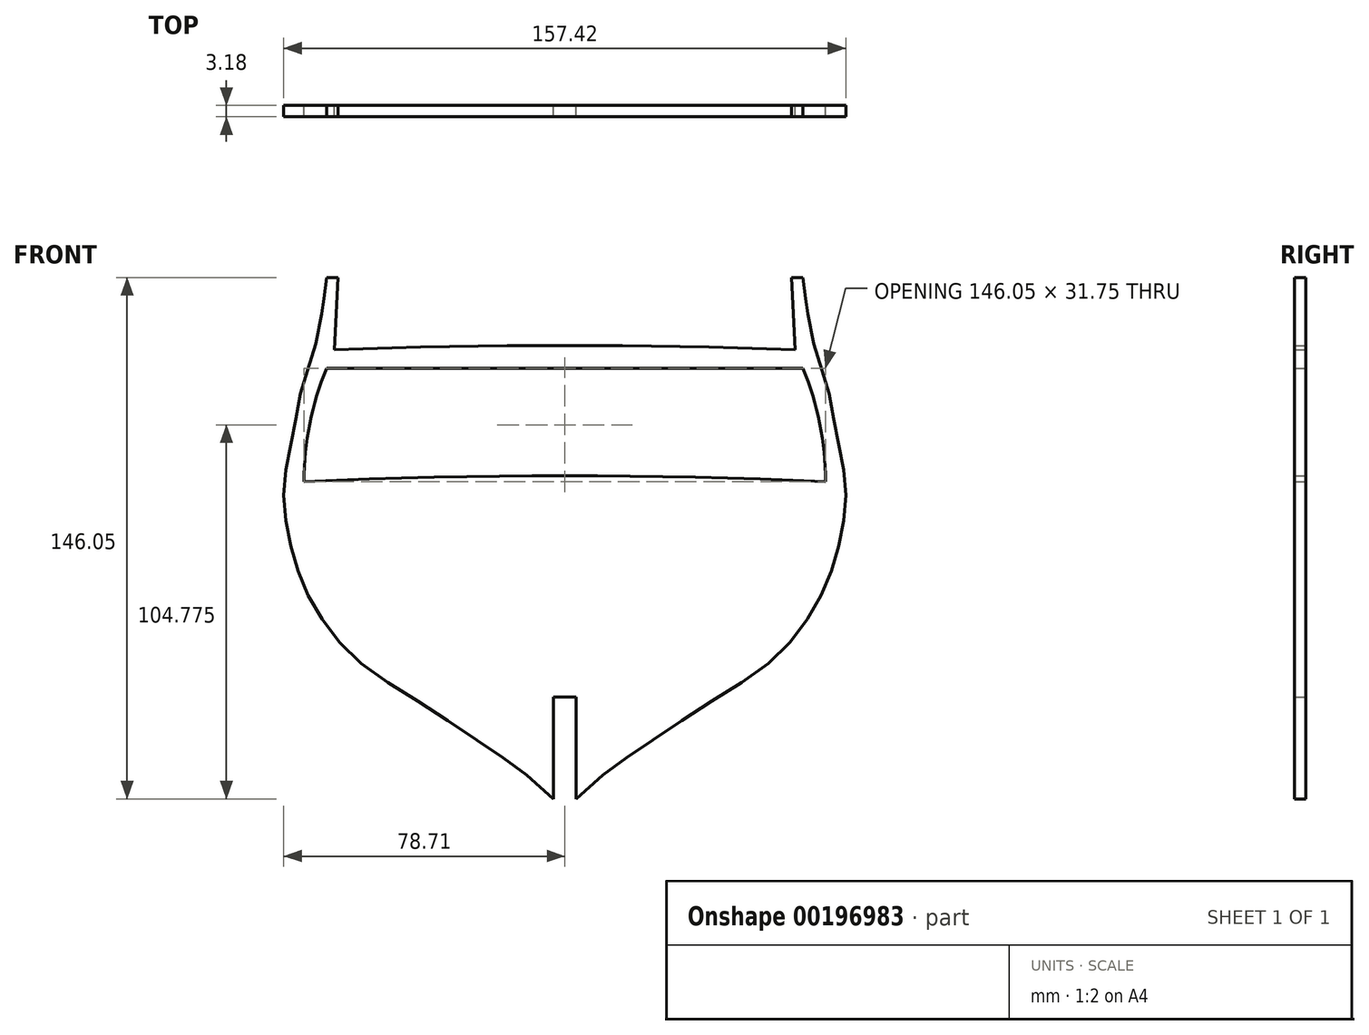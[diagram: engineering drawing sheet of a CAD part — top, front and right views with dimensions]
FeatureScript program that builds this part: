
annotation { "Feature Type Name" : "Feature", "Feature Type Description" : "" }
export const myFeature = defineFeature(function(context is Context, id is Id, definition is map)
    precondition{}
    {
        {
            var Q0;
            Q0=qCreatedBy(makeId("Front.planeOp"),FACE);
            var sketch = newSketch(context, id + "F0", { "sketchPlane" : qUnion([Q0])});
            skLineSegment(sketch, "E0", {"start": v(0, 0) * mm, "end": v(0, -60.33) * mm, "construction": true});
            skLineSegment(sketch, "E1", {"start": v(0, -60.33) * mm, "end": v(3.18, -60.33) * mm});
            skLineSegment(sketch, "E2", {"start": v(3.18, -60.33) * mm, "end": v(3.18, -88.9) * mm});
            skLineSegment(sketch, "E3", {"start": v(3.18, -88.9) * mm, "end": v(-3.18, -88.9) * mm, "construction": true});
            skLineSegment(sketch, "E4", {"start": v(-3.18, -88.9) * mm, "end": v(-3.18, -60.33) * mm});
            skLineSegment(sketch, "E5", {"start": v(-3.18, -60.33) * mm, "end": v(0, -60.33) * mm});
            skLineSegment(sketch, "E6", {"start": v(0, 0) * mm, "end": v(0, 31.75) * mm, "construction": true});
            skLineSegment(sketch, "E7", {"start": v(0, 31.75) * mm, "end": v(0, 38.1) * mm, "construction": true});
            skLineSegment(sketch, "E8", {"start": v(0, 31.75) * mm, "end": v(66.68, 31.75) * mm});
            skLineSegment(sketch, "E9", {"start": v(66.68, 31.75) * mm, "end": v(73.03, 0) * mm, "construction": true});
            skLineSegment(sketch, "E10", {"start": v(73.03, 0) * mm, "end": v(0, 0) * mm, "construction": true});
            skLineSegment(sketch, "E11", {"start": v(0, 0) * mm, "end": v(-73.03, 0) * mm, "construction": true});
            skLineSegment(sketch, "E12", {"start": v(-73.03, 0) * mm, "end": v(-66.68, 31.75) * mm, "construction": true});
            skLineSegment(sketch, "E13", {"start": v(-66.68, 31.75) * mm, "end": v(0, 31.75) * mm});
            skArc(sketch, "E14", {"start": v(-66.67, 31.75) * mm, "mid": v(-71.4, 16.19) * mm, "end": v(-73.03, 0) * mm});
            skArc(sketch, "E15", {"start": v(73.02, 0) * mm, "mid": v(71.4, 16.19) * mm, "end": v(66.67, 31.75) * mm});
            skPoint(sketch, "E16", {"position": v(-71.4, 16.19) * mm});
            skPoint(sketch, "E17", {"position": v(71.4, 16.19) * mm});
            skArc(sketch, "E18", {"start": v(73.02, 0) * mm, "mid": v(0, 1.59) * mm, "end": v(-73.03, 0) * mm});
            skPoint(sketch, "E19", {"position": v(0, 1.59) * mm});
            skArc(sketch, "E20", {"start": v(64.55, 36.88) * mm, "mid": v(0, 38.1) * mm, "end": v(-64.55, 36.88) * mm});
            skLineSegment(sketch, "E21", {"start": v(-66.68, 31.75) * mm, "end": v(-64.55, 36.88) * mm, "construction": true});
            skLineSegment(sketch, "E22", {"start": v(66.68, 31.75) * mm, "end": v(64.55, 36.88) * mm, "construction": true});
            skFitSpline(sketch, "E23", {"points": [v(3.17, -88.9) * mm, v(19.05, -76.2) * mm, v(38.1, -63.5) * mm, v(57.15, -50.8) * mm, v(68.26, -38.1) * mm, v(74.61, -25.4) * mm, v(77.79, -12.7) * mm, v(78.58, 0) * mm, v(76.2, 12.7) * mm, v(73.82, 25.4) * mm, v(69.85, 38.1) * mm, v(67.47, 50.8) * mm, v(66.68, 57.15) * mm], "startDerivative": vector(194.78, 194.78) * mm, "endDerivative": vector(-43.4, 347.17) * mm});
            skLineSegment(sketch, "E24", {"start": v(66.68, 57.15) * mm, "end": v(63.5, 57.15) * mm});
            skLineSegment(sketch, "E25", {"start": v(63.5, 57.15) * mm, "end": v(64.55, 36.88) * mm});
            skLineSegment(sketch, "E26.MirrorCS", {"start": v(-66.68, 57.15) * mm, "end": v(-63.5, 57.15) * mm});
            skLineSegment(sketch, "E27.MirrorCS", {"start": v(-63.5, 57.15) * mm, "end": v(-64.55, 36.88) * mm});
            skFitSpline(sketch, "E28.MirrorCS", {"points": [v(-3.17, -88.9) * mm, v(-19.05, -76.2) * mm, v(-38.1, -63.5) * mm, v(-57.15, -50.8) * mm, v(-68.26, -38.1) * mm, v(-74.61, -25.4) * mm, v(-77.79, -12.7) * mm, v(-78.58, 0) * mm, v(-76.2, 12.7) * mm, v(-73.82, 25.4) * mm, v(-69.85, 38.1) * mm, v(-67.47, 50.8) * mm, v(-66.68, 57.15) * mm], "startDerivative": vector(-194.78, 194.78) * mm, "endDerivative": vector(43.4, 347.17) * mm});
            skSolve(sketch);
        }
        {
            var Q0;
            Q0=makeQuery(id+"F0.imprint","IMPRINT",FACE,{"disambiguationData":[TD([[makeQuery(id+"F0.imprint","IMPRINT",EDGE,{"derivedFrom":sQuery(id+"F0.wireOp",EDGE,"E1")}),1.0]])]});
            extrude(context, id + "F1", {"entities" : qUnion([Q0]), "endBound" : BoundingType.SYMMETRIC, "depth" : 3.17 * mm});
        }
    });
